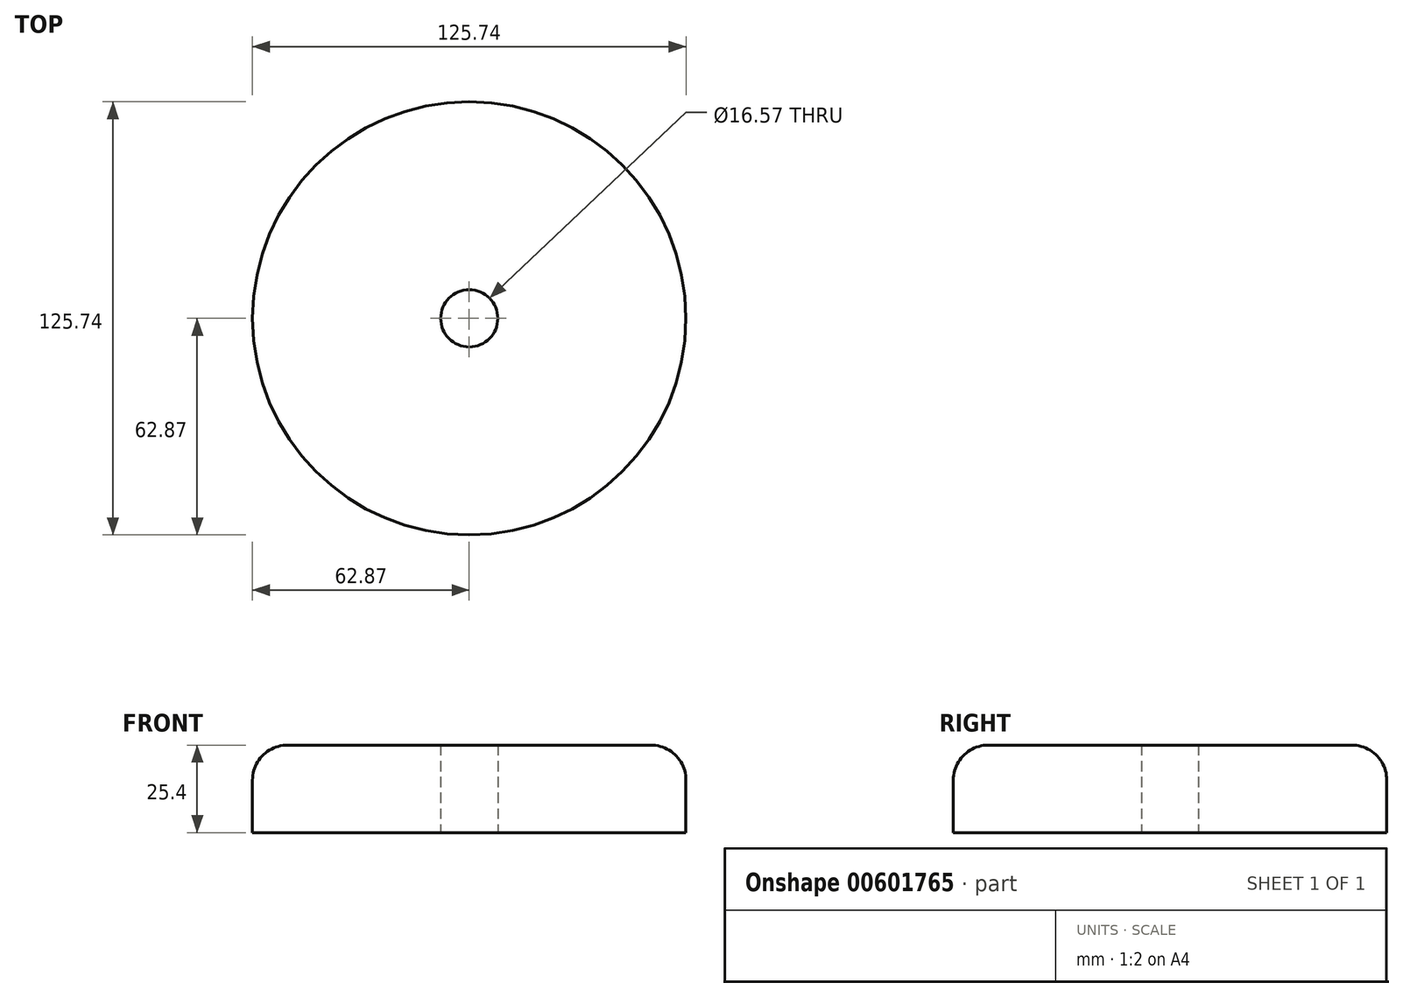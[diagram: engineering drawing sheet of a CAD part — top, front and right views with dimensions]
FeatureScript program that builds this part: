
annotation { "Feature Type Name" : "Feature", "Feature Type Description" : "" }
export const myFeature = defineFeature(function(context is Context, id is Id, definition is map)
    precondition{}
    {
        {
            var Q0;
            Q0=qCreatedBy(makeId("Top.planeOp"),FACE);
            var sketch = newSketch(context, id + "F0", { "sketchPlane" : qUnion([Q0])});
            skCircle(sketch, "E0", {"center": v(0, 0) * mm, "radius": 62.87 * mm});
            skCircle(sketch, "E1", {"center": v(0, 0) * mm, "radius": 8.28 * mm});
            skSolve(sketch);
        }
        {
            var Q0;
            Q0 = qSketchRegion(id + "F0", true);
            extrude(context, id + "F1", {"entities" : qUnion([Q0]), "depth" : 25.4 * mm, "offsetDistance" : 25.4 * mm});
        }
        {
            var Q0;
            Q0=sQuery(id+"F0.wireOp",EDGE,"E1");
            extrude(context, id + "F2", {"bodyType" : ToolBodyType.SURFACE, "surfaceEntities" : qUnion([Q0]), "depth" : 152.4 * mm, "offsetDistance" : 25.4 * mm});
        }
        {
            var Q0;
            Q0=makeQuery(id+"F1.opExtrude","CAP_EDGE",EDGE,{"disambiguationData":[OSD([sQuery(id+"F0.wireOp",EDGE,"E0")])],"isStart":false});
            fillet(context, id + "F3", {"entities" : qUnion([Q0]), "radius" : 10.16 * mm, "tangentPropagation" : true, "allowEdgeOverflow" : false});
        }
    });
